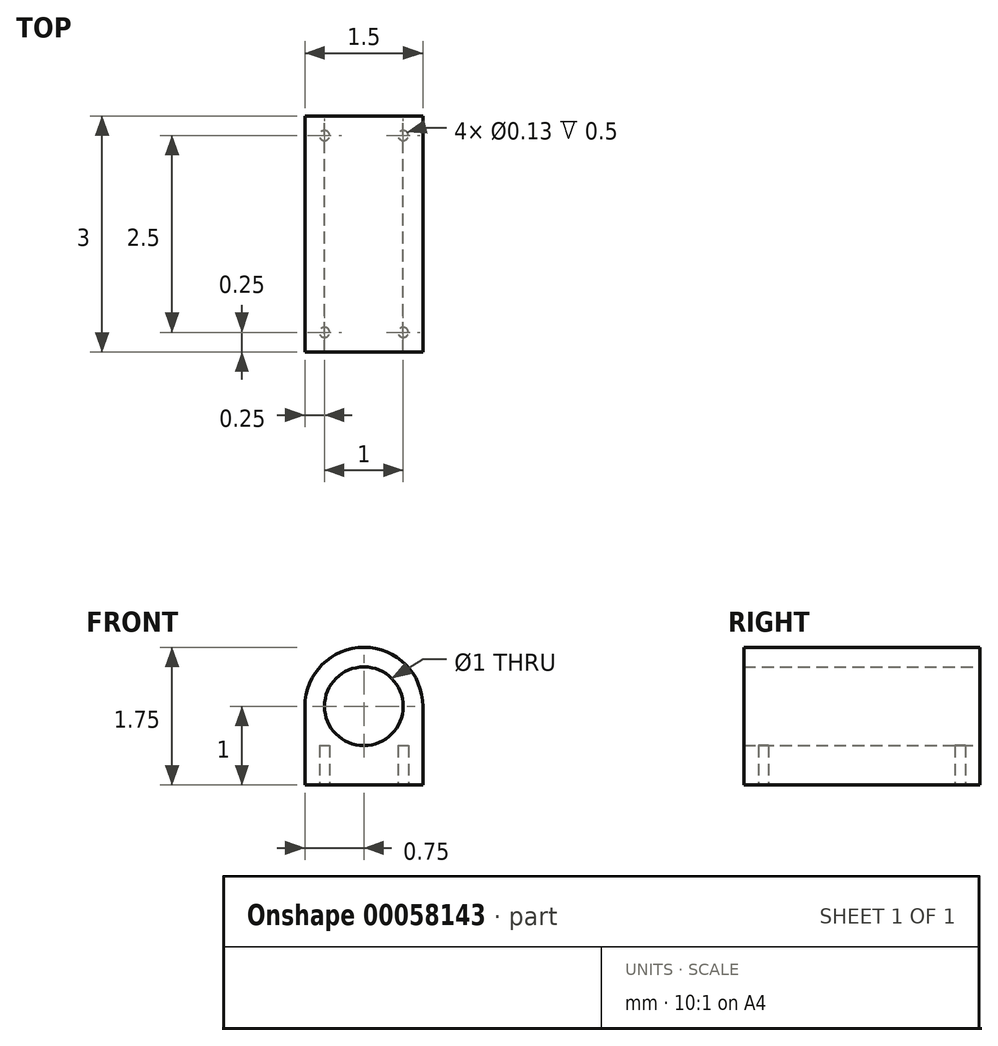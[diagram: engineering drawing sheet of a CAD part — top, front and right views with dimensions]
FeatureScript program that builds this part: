
annotation { "Feature Type Name" : "Feature", "Feature Type Description" : "" }
export const myFeature = defineFeature(function(context is Context, id is Id, definition is map)
    precondition{}
    {
        {
            var Q0;
            Q0=qCreatedBy(makeId("Front.planeOp"),FACE);
            var sketch = newSketch(context, id + "F0", { "sketchPlane" : qUnion([Q0])});
            skLineSegment(sketch, "E0.top", {"start": v(-0.75, -1) * mm, "end": v(0.75, -1) * mm});
            skLineSegment(sketch, "E0.left", {"start": v(-0.75, 0) * mm, "end": v(-0.75, -1) * mm});
            skLineSegment(sketch, "E0.right", {"start": v(0.75, 0) * mm, "end": v(0.75, -1) * mm});
            skArc(sketch, "E1", {"start": v(0.75, 0) * mm, "mid": v(0, 0.75) * mm, "end": v(-0.75, 0) * mm});
            skCircle(sketch, "E2", {"center": v(0, 0) * mm, "radius": 0.5 * mm});
            skSolve(sketch);
        }
        {
            var Q0;
            Q0 = qSketchRegion(id + "F0", true);
            extrude(context, id + "F1", {"entities" : qUnion([Q0]), "depth" : 1.5 * mm, "hasSecondDirection" : true, "secondDirectionOppositeDirection" : true, "secondDirectionDepth" : 1.5 * mm});
        }
        {
            var Q0;
            Q0=makeQuery(id+"F1.opExtrude","SWEPT_FACE",FACE,{"disambiguationData":[OSD([sQuery(id+"F0.wireOp",EDGE,"E0.top")])]});
            var sketch = newSketch(context, id + "F2", { "sketchPlane" : qUnion([Q0])});
            skCircle(sketch, "E3", {"center": v(0.5, 1.25) * mm, "radius": 0.07 * mm});
            skCircle(sketch, "E4", {"center": v(-0.5, 1.25) * mm, "radius": 0.07 * mm});
            skCircle(sketch, "E5", {"center": v(-0.5, -1.25) * mm, "radius": 0.07 * mm});
            skCircle(sketch, "E6", {"center": v(0.5, -1.25) * mm, "radius": 0.07 * mm});
            skLineSegment(sketch, "E7", {"start": v(0, 1.5) * mm, "end": v(-0.1, 2.47) * mm});
            skSolve(sketch);
        }
        {
            var Q0;
            Q0=makeQuery(id+"F2.imprint","IMPRINT",FACE,{"disambiguationData":[TD([[makeQuery(id+"F2.imprint","IMPRINT",EDGE,{"derivedFrom":sQuery(id+"F2.wireOp",EDGE,"E5")}),1.0]])]});
            var Q1;
            Q1=makeQuery(id+"F2.imprint","IMPRINT",FACE,{"disambiguationData":[TD([[makeQuery(id+"F2.imprint","IMPRINT",EDGE,{"derivedFrom":sQuery(id+"F2.wireOp",EDGE,"E6")}),1.0]])]});
            var Q2;
            Q2=makeQuery(id+"F2.imprint","IMPRINT",FACE,{"disambiguationData":[TD([[makeQuery(id+"F2.imprint","IMPRINT",EDGE,{"derivedFrom":sQuery(id+"F2.wireOp",EDGE,"E3")}),1.0]])]});
            var Q3;
            Q3=makeQuery(id+"F2.imprint","IMPRINT",FACE,{"disambiguationData":[TD([[makeQuery(id+"F2.imprint","IMPRINT",EDGE,{"derivedFrom":sQuery(id+"F2.wireOp",EDGE,"E4")}),1.0]])]});
            extrude(context, id + "F3", {"entities" : qUnion([Q0, Q1, Q2, Q3]), "operationType" : NewBodyOperationType.REMOVE, "oppositeDirection" : true, "depth" : 0.5 * mm});
        }
    });
